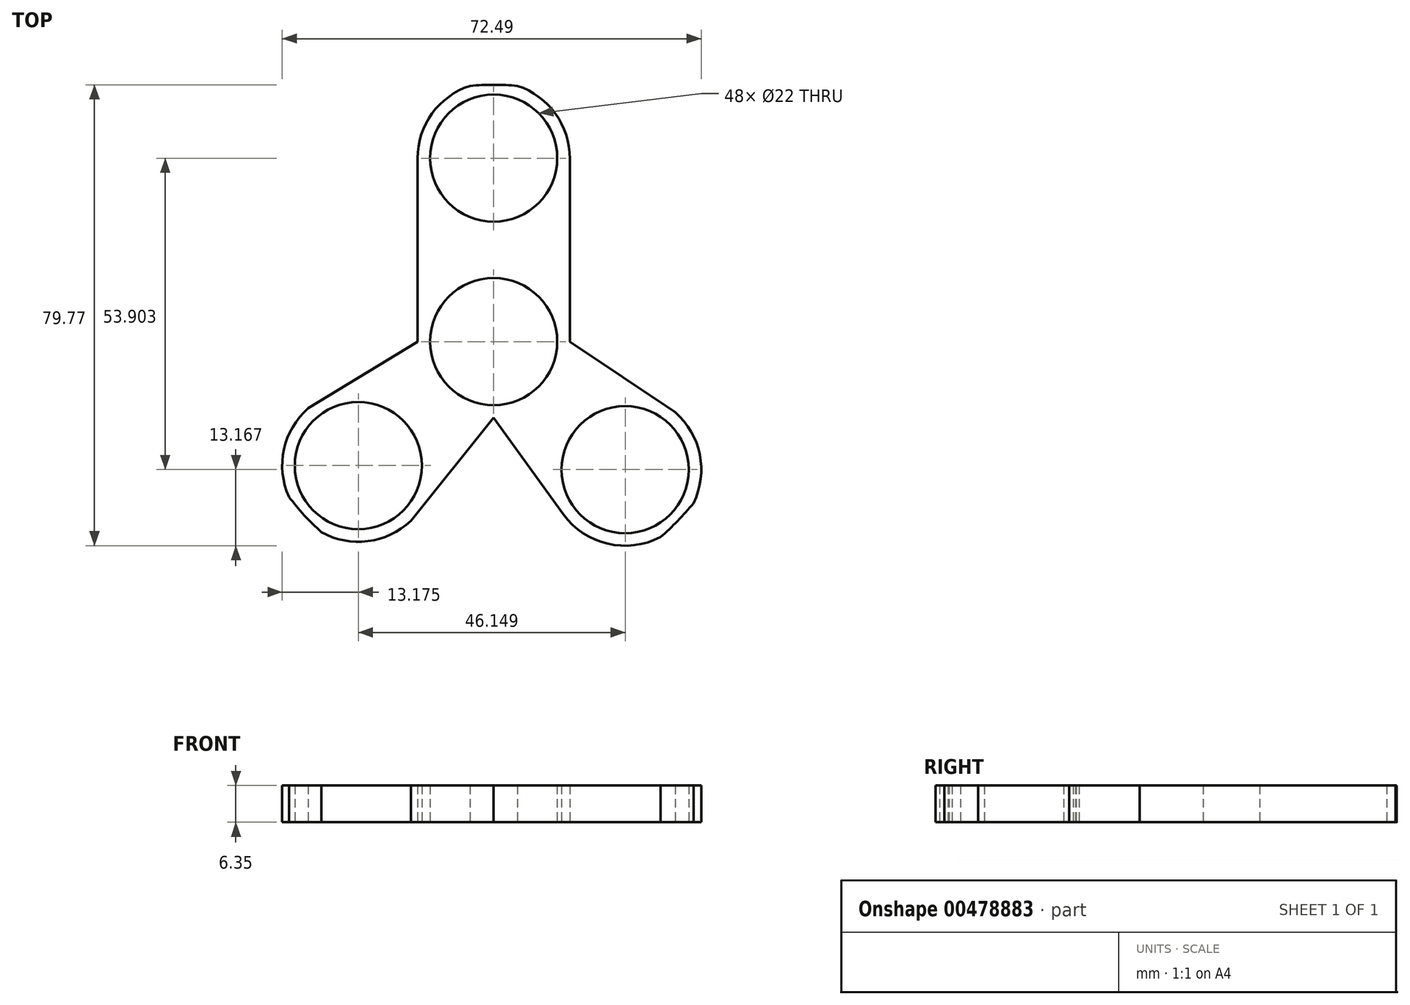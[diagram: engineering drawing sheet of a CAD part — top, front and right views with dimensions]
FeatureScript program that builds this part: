
annotation { "Feature Type Name" : "Feature", "Feature Type Description" : "" }
export const myFeature = defineFeature(function(context is Context, id is Id, definition is map)
    precondition{}
    {
        {
            var Q0;
            Q0=qCreatedBy(makeId("Top.planeOp"),FACE);
            var sketch = newSketch(context, id + "F0", { "sketchPlane" : qUnion([Q0])});
            skCircle(sketch, "E0", {"center": v(0, 0) * mm, "radius": 44.45 * mm});
            skCircle(sketch, "E1", {"center": v(0, 0) * mm, "radius": 11 * mm});
            skCircle(sketch, "E2", {"center": v(0, 0) * mm, "radius": 13.16 * mm});
            skLineSegment(sketch, "E3", {"start": v(0, 0) * mm, "end": v(0, 31.75) * mm});
            skCircle(sketch, "E4", {"center": v(0, 31.75) * mm, "radius": 11 * mm});
            skCircle(sketch, "E5", {"center": v(0, 31.75) * mm, "radius": 13.16 * mm});
            skLineSegment(sketch, "E6", {"start": v(0, 0) * mm, "end": v(-23.4, -21.45) * mm});
            skLineSegment(sketch, "E7", {"start": v(0, 0) * mm, "end": v(22.74, -22.15) * mm});
            skCircle(sketch, "E8", {"center": v(-23.4, -21.45) * mm, "radius": 11 * mm});
            skCircle(sketch, "E9", {"center": v(22.74, -22.15) * mm, "radius": 11 * mm});
            skCircle(sketch, "E10", {"center": v(22.74, -22.15) * mm, "radius": 13.16 * mm});
            skCircle(sketch, "E11", {"center": v(-23.4, -21.45) * mm, "radius": 13.17 * mm});
            skLineSegment(sketch, "E12", {"start": v(-13.16, 31.75) * mm, "end": v(-13.16, 0) * mm});
            skLineSegment(sketch, "E13", {"start": v(-13.16, 0) * mm, "end": v(-32.07, -11.54) * mm});
            skLineSegment(sketch, "E14", {"start": v(-14.34, -31.01) * mm, "end": v(0, -13.16) * mm});
            skLineSegment(sketch, "E15", {"start": v(0, -13.16) * mm, "end": v(12.08, -29.87) * mm});
            skLineSegment(sketch, "E16", {"start": v(31.4, -12.23) * mm, "end": v(13.16, 0) * mm});
            skLineSegment(sketch, "E17", {"start": v(13.16, 0) * mm, "end": v(13.16, 31.65) * mm});
            skSolve(sketch);
        }
        {
            var Q0;
            {var subQ0=sQuery(id+"F0.wireOp",EDGE,"E12");Q0=makeQuery(id+"F0.imprint","IMPRINT",FACE,{"disambiguationData":[TD([[makeQuery(id+"F0.imprint","IMPRINT",EDGE,{"derivedFrom":subQ0}),1.0]])]});}
            var Q1;
            {var subQ0=sQuery(id+"F0.wireOp",EDGE,"E17");Q1=makeQuery(id+"F0.imprint","IMPRINT",FACE,{"disambiguationData":[TD([[makeQuery(id+"F0.imprint","IMPRINT",EDGE,{"derivedFrom":subQ0}),1.0]])]});}
            var Q2;
            Q2=makeQuery(id+"F0.imprint","IMPRINT",FACE,{"disambiguationData":[TD([[makeQuery(id+"F0.imprint","IMPRINT",EDGE,{"derivedFrom":sQuery(id+"F0.wireOp",EDGE,"E4")}),-1.0]])]});
            var Q3;
            {var subQ3=sQuery(id+"F0.wireOp",EDGE,"E7");var subQ5=sQuery(id+"F0.wireOp",EDGE,"E10");var subQ6=makeQuery(id+"F0.imprint","INTERSECT",VERTEX,{"derivedFrom":[subQ3,subQ5]});Q3=makeQuery(id+"F0.imprint","IMPRINT",FACE,{"disambiguationData":[TD([[makeQuery(id+"F0.imprint","IMPRINT",EDGE,{"disambiguationData":[TD([[subQ6,1.0]])],"derivedFrom":subQ3}),1.0]])]});}
            var Q4;
            {var subQ0=sQuery(id+"F0.wireOp",EDGE,"E15");Q4=makeQuery(id+"F0.imprint","IMPRINT",FACE,{"disambiguationData":[TD([[makeQuery(id+"F0.imprint","IMPRINT",EDGE,{"derivedFrom":subQ0}),1.0]])]});}
            var Q5;
            {var subQ3=sQuery(id+"F0.wireOp",EDGE,"E6");var subQ5=sQuery(id+"F0.wireOp",EDGE,"E11");var subQ6=makeQuery(id+"F0.imprint","INTERSECT",VERTEX,{"derivedFrom":[subQ3,subQ5]});Q5=makeQuery(id+"F0.imprint","IMPRINT",FACE,{"disambiguationData":[TD([[makeQuery(id+"F0.imprint","IMPRINT",EDGE,{"disambiguationData":[TD([[subQ6,1.0]])],"derivedFrom":subQ3}),1.0]])]});}
            var Q6;
            {var subQ3=sQuery(id+"F0.wireOp",EDGE,"E6");var subQ5=sQuery(id+"F0.wireOp",EDGE,"E11");var subQ6=makeQuery(id+"F0.imprint","INTERSECT",VERTEX,{"derivedFrom":[subQ3,subQ5]});Q6=makeQuery(id+"F0.imprint","IMPRINT",FACE,{"disambiguationData":[TD([[makeQuery(id+"F0.imprint","IMPRINT",EDGE,{"disambiguationData":[TD([[subQ6,1.0]])],"derivedFrom":subQ3}),-1.0]])]});}
            var Q7;
            Q7=makeQuery(id+"F0.imprint","IMPRINT",FACE,{"disambiguationData":[TD([[makeQuery(id+"F0.imprint","IMPRINT",EDGE,{"derivedFrom":sQuery(id+"F0.wireOp",EDGE,"E8")}),-1.0]])]});
            var Q8;
            Q8=makeQuery(id+"F0.imprint","IMPRINT",FACE,{"disambiguationData":[TD([[makeQuery(id+"F0.imprint","IMPRINT",EDGE,{"derivedFrom":sQuery(id+"F0.wireOp",EDGE,"E9")}),-1.0]])]});
            var Q9;
            {var subQ4=sQuery(id+"F0.wireOp",EDGE,"E1");var subQ6=sQuery(id+"F0.wireOp",EDGE,"E6");var subQ8=makeQuery(id+"F0.imprint","INTERSECT",VERTEX,{"derivedFrom":[subQ4,subQ6]});Q9=makeQuery(id+"F0.imprint","IMPRINT",FACE,{"disambiguationData":[TD([[makeQuery(id+"F0.imprint","IMPRINT",EDGE,{"disambiguationData":[TD([[subQ8,1.0]])],"derivedFrom":subQ4}),-1.0]])]});}
            var Q10;
            {var subQ0=sQuery(id+"F0.wireOp",EDGE,"E3");var subQ1=sQuery(id+"F0.wireOp",EDGE,"E1");var subQ2=makeQuery(id+"F0.imprint","INTERSECT",VERTEX,{"derivedFrom":[subQ1,subQ0]});Q10=makeQuery(id+"F0.imprint","IMPRINT",FACE,{"disambiguationData":[TD([[makeQuery(id+"F0.imprint","IMPRINT",EDGE,{"disambiguationData":[TD([[subQ2,1.0]])],"derivedFrom":subQ1}),-1.0]])]});}
            var Q11;
            {var subQ0=sQuery(id+"F0.wireOp",EDGE,"E6");var subQ1=sQuery(id+"F0.wireOp",EDGE,"E1");var subQ2=makeQuery(id+"F0.imprint","INTERSECT",VERTEX,{"derivedFrom":[subQ1,subQ0]});Q11=makeQuery(id+"F0.imprint","IMPRINT",FACE,{"disambiguationData":[TD([[makeQuery(id+"F0.imprint","IMPRINT",EDGE,{"disambiguationData":[TD([[subQ2,-1.0]])],"derivedFrom":subQ1}),-1.0]])]});}
            extrude(context, id + "F1", {"entities" : qUnion([Q0, Q1, Q2, Q3, Q4, Q5, Q6, Q7, Q8, Q9, Q10, Q11]), "depth" : 6.35 * mm});
        }
    });
